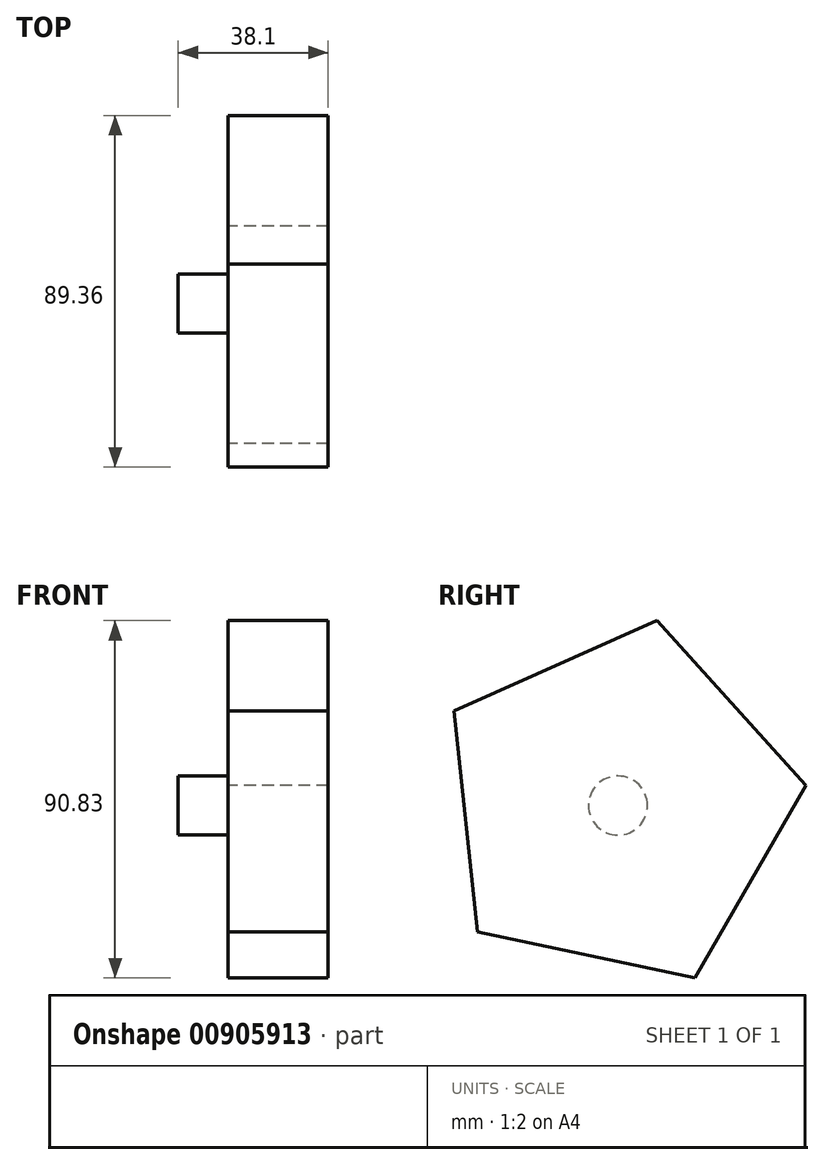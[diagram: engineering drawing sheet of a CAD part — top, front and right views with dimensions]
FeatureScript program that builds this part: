
annotation { "Feature Type Name" : "Feature", "Feature Type Description" : "" }
export const myFeature = defineFeature(function(context is Context, id is Id, definition is map)
    precondition{}
    {
        {
            var Q0;
            Q0=qCreatedBy(makeId("Right.planeOp"),FACE);
            var sketch = newSketch(context, id + "F0", { "sketchPlane" : qUnion([Q0])});
            skCircle(sketch, "E0.cCircle", {"center": v(0, 0) * mm, "radius": 38.85 * mm, "construction": true});
            skLineSegment(sketch, "E0.0", {"start": v(47.75, 5.06) * mm, "end": v(19.57, -43.85) * mm});
            skLineSegment(sketch, "E0.1", {"start": v(19.57, -43.85) * mm, "end": v(-35.65, -32.16) * mm});
            skLineSegment(sketch, "E0.2", {"start": v(-35.65, -32.16) * mm, "end": v(-41.6, 23.97) * mm});
            skLineSegment(sketch, "E0.3", {"start": v(-41.6, 23.97) * mm, "end": v(9.94, 46.98) * mm});
            skLineSegment(sketch, "E0.4", {"start": v(9.94, 46.98) * mm, "end": v(47.75, 5.06) * mm});
            skPoint(sketch, "E0.0.midPoint", {"position": v(33.66, -19.4) * mm});
            skSolve(sketch);
        }
        {
            var Q0;
            Q0 = qSketchRegion(id + "F0", true);
            extrude(context, id + "F1", {"entities" : qUnion([Q0]), "depth" : 25.4 * mm, "offsetDistance" : 25.4 * mm});
        }
        {
            var Q0;
            Q0=makeQuery(id+"F1.opExtrude","CAP_FACE",FACE,{"disambiguationData":[OSD([sQuery(id+"F0.wireOp",EDGE,"E0.0"),sQuery(id+"F0.wireOp",EDGE,"E0.1"),sQuery(id+"F0.wireOp",EDGE,"E0.2"),sQuery(id+"F0.wireOp",EDGE,"E0.3"),sQuery(id+"F0.wireOp",EDGE,"E0.4")])],"isStart":true});
            var sketch = newSketch(context, id + "F2", { "sketchPlane" : qUnion([Q0])});
            skCircle(sketch, "E1", {"center": v(0, 0) * mm, "radius": 7.49 * mm});
            skSolve(sketch);
        }
        {
            var Q0;
            Q0=makeQuery(id+"F2.imprint","IMPRINT",FACE,{"disambiguationData":[TD([[makeQuery(id+"F2.imprint","IMPRINT",EDGE,{"derivedFrom":sQuery(id+"F2.wireOp",EDGE,"E1")}),1.0]])]});
            extrude(context, id + "F3", {"entities" : qUnion([Q0]), "operationType" : NewBodyOperationType.ADD, "depth" : 12.7 * mm, "offsetDistance" : 25.4 * mm});
        }
    });
